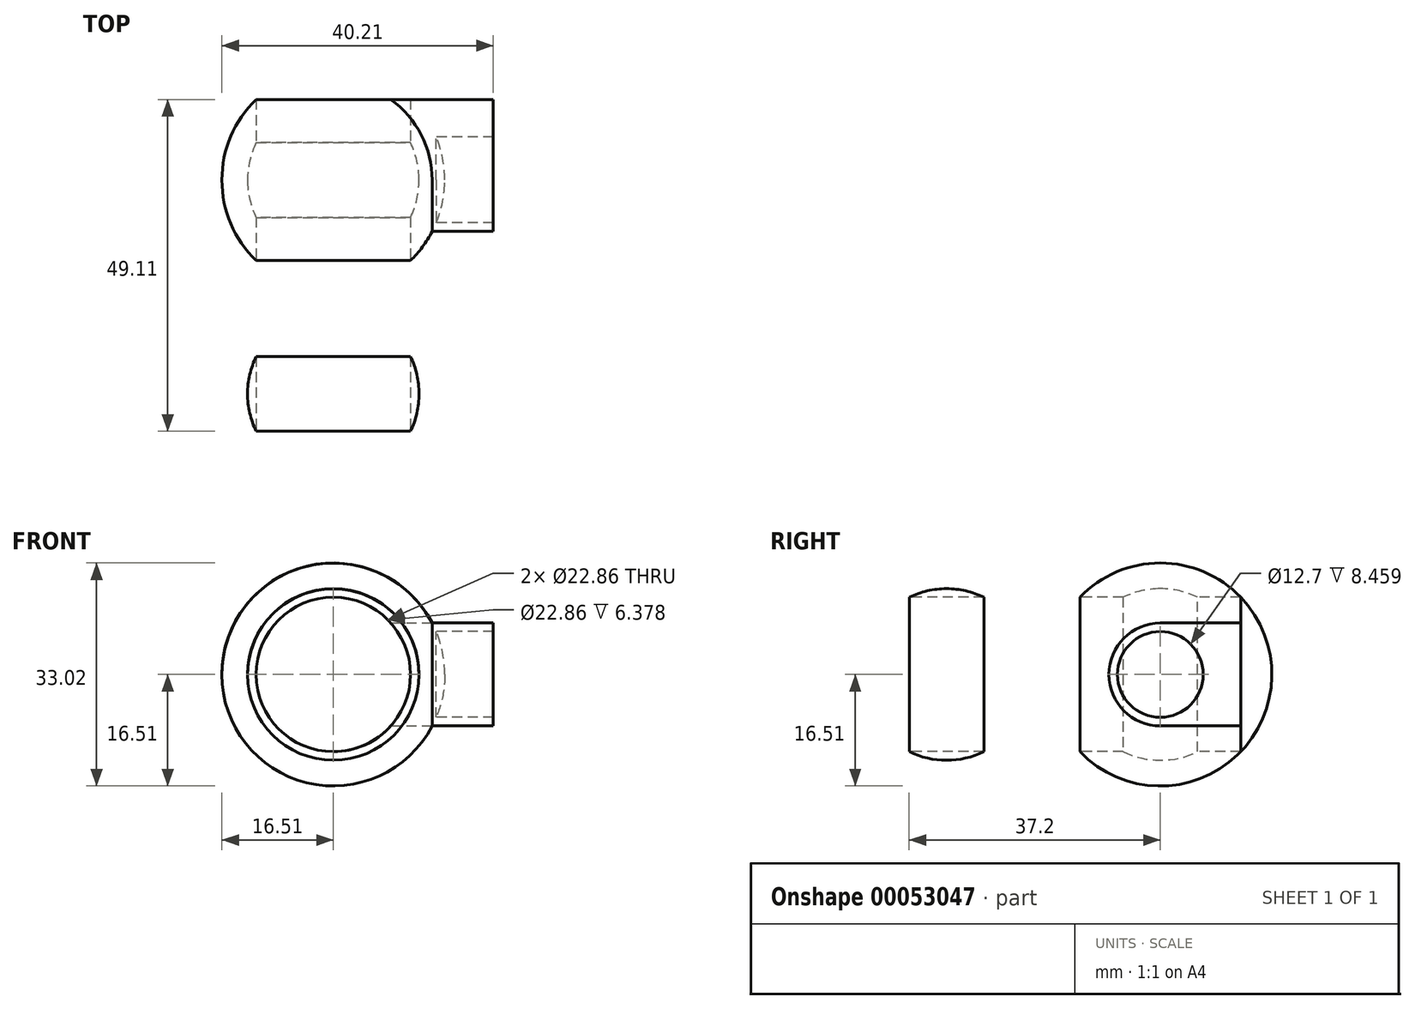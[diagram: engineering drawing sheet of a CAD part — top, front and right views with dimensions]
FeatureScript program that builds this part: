
annotation { "Feature Type Name" : "Feature", "Feature Type Description" : "" }
export const myFeature = defineFeature(function(context is Context, id is Id, definition is map)
    precondition{}
    {
        {
            var Q0;
            Q0=qCreatedBy(makeId("Front.planeOp"),FACE);
            var sketch = newSketch(context, id + "F0", { "sketchPlane" : qUnion([Q0])});
            skCircle(sketch, "E0", {"center": v(0, 0) * mm, "radius": 12.7 * mm});
            skLineSegment(sketch, "E1.rect.top", {"start": v(23.7, 6.35) * mm, "end": v(11, 6.35) * mm});
            skLineSegment(sketch, "E1.rect.left", {"start": v(23.7, 0) * mm, "end": v(23.7, 6.35) * mm});
            skLineSegment(sketch, "E2", {"start": v(-12.7, 0) * mm, "end": v(23.7, 0) * mm});
            skArc(sketch, "E3", {"start": v(13.97, 0) * mm, "mid": v(0, 13.97) * mm, "end": v(-13.97, 0) * mm});
            skArc(sketch, "E4", {"start": v(16.51, 0) * mm, "mid": v(0, 16.51) * mm, "end": v(-16.51, 0) * mm});
            skLineSegment(sketch, "E5", {"start": v(-12.7, 0) * mm, "end": v(-16.51, 0) * mm});
            skPoint(sketch, "E6", {"position": v(13.97, 0) * mm});
            skPoint(sketch, "E7", {"position": v(16.51, 0) * mm});
            skLineSegment(sketch, "E8", {"start": v(10.16, 7.62) * mm, "end": v(23.7, 7.62) * mm});
            skLineSegment(sketch, "E9", {"start": v(23.7, 7.62) * mm, "end": v(23.7, 6.35) * mm});
            skCircle(sketch, "E10", {"center": v(0, 0) * mm, "radius": 11.43 * mm});
            skSolve(sketch);
        }
        {
            var Q0;
            {var subQ0=sQuery(id+"F0.wireOp",EDGE,"E1.rect.top");var subQ1=sQuery(id+"F0.wireOp",EDGE,"E0");var subQ2=makeQuery(id+"F0.imprint","INTERSECT",VERTEX,{"derivedFrom":[subQ1,subQ0]});Q0=makeQuery(id+"F0.imprint","IMPRINT",FACE,{"disambiguationData":[TD([[makeQuery(id+"F0.imprint","IMPRINT",EDGE,{"disambiguationData":[TD([[subQ2,1.0]])],"derivedFrom":subQ1}),-1.0]])]});}
            var Q1;
            {var subQ0=sQuery(id+"F0.wireOp",EDGE,"E4");var subQ1=sQuery(id+"F0.wireOp",EDGE,"E1.rect.top");var subQ2=makeQuery(id+"F0.imprint","INTERSECT",VERTEX,{"derivedFrom":[subQ1,subQ0]});Q1=makeQuery(id+"F0.imprint","IMPRINT",FACE,{"disambiguationData":[TD([[makeQuery(id+"F0.imprint","IMPRINT",EDGE,{"disambiguationData":[TD([[subQ2,-1.0]])],"derivedFrom":subQ1}),1.0]])]});}
            var Q2;
            {var subQ0=sQuery(id+"F0.wireOp",EDGE,"E1.rect.top");var subQ1=sQuery(id+"F0.wireOp",EDGE,"E0");var subQ2=makeQuery(id+"F0.imprint","INTERSECT",VERTEX,{"derivedFrom":[subQ1,subQ0]});Q2=makeQuery(id+"F0.imprint","IMPRINT",FACE,{"disambiguationData":[TD([[makeQuery(id+"F0.imprint","IMPRINT",EDGE,{"disambiguationData":[TD([[subQ2,1.0]])],"derivedFrom":subQ0}),-1.0]])]});}
            var Q3;
            {var subQ0=sQuery(id+"F0.wireOp",EDGE,"E4");var subQ1=sQuery(id+"F0.wireOp",EDGE,"E1.rect.top");var subQ2=makeQuery(id+"F0.imprint","INTERSECT",VERTEX,{"derivedFrom":[subQ1,subQ0]});Q3=makeQuery(id+"F0.imprint","IMPRINT",FACE,{"disambiguationData":[TD([[makeQuery(id+"F0.imprint","IMPRINT",EDGE,{"disambiguationData":[TD([[subQ2,-1.0]])],"derivedFrom":subQ1}),-1.0]])]});}
            var Q4;
            {var subQ0=sQuery(id+"F0.wireOp",EDGE,"E9");Q4=makeQuery(id+"F0.imprint","IMPRINT",FACE,{"disambiguationData":[TD([[makeQuery(id+"F0.imprint","IMPRINT",EDGE,{"derivedFrom":subQ0}),-1.0]])]});}
            var Q5;
            {var subQ0=sQuery(id+"F0.wireOp",EDGE,"E5");var subQ5=sQuery(id+"F0.wireOp",EDGE,"E3");var subQ6=makeQuery(id+"F0.imprint","INTERSECT",VERTEX,{"derivedFrom":[subQ5,subQ0]});Q5=makeQuery(id+"F0.imprint","IMPRINT",FACE,{"disambiguationData":[TD([[makeQuery(id+"F0.imprint","IMPRINT",EDGE,{"disambiguationData":[TD([[subQ6,1.0]])],"derivedFrom":subQ5}),1.0]])]});}
            var Q6;
            {var subQ0=sQuery(id+"F0.wireOp",EDGE,"E5");var subQ1=sQuery(id+"F0.wireOp",EDGE,"E3");var subQ2=makeQuery(id+"F0.imprint","INTERSECT",VERTEX,{"derivedFrom":[subQ1,subQ0]});Q6=makeQuery(id+"F0.imprint","IMPRINT",FACE,{"disambiguationData":[TD([[makeQuery(id+"F0.imprint","IMPRINT",EDGE,{"disambiguationData":[TD([[subQ2,1.0]])],"derivedFrom":subQ1}),-1.0]])]});}
            var Q7;
            Q7=sQuery(id+"F0.wireOp",EDGE,"E2");
            revolve(context, id + "F1", {"entities" : qUnion([Q0, Q1, Q2, Q3, Q4, Q5, Q6]), "axis" : qUnion([Q7]), "revolveType" : RevolveType.FULL});
        }
        {
            var Q0;
            {var subQ0=sQuery(id+"F0.wireOp",EDGE,"E0");var subQ1=makeQuery(id+"F0.imprint","INTERSECT",VERTEX,{"derivedFrom":[subQ0,sQuery(id+"F0.wireOp",EDGE,"E1.rect.top")]});Q0=makeQuery(id+"F0.imprint","IMPRINT",FACE,{"disambiguationData":[TD([[makeQuery(id+"F0.imprint","IMPRINT",EDGE,{"disambiguationData":[TD([[subQ1,1.0]])],"derivedFrom":subQ0}),1.0]])]});}
            var Q1;
            Q1=sQuery(id+"F0.wireOp",EDGE,"E2");
            revolve(context, id + "F2", {"entities" : qUnion([Q0]), "axis" : qUnion([Q1]), "revolveType" : RevolveType.FULL});
        }
        {
            var Q0;
            {var subQ0=sQuery(id+"F0.wireOp",EDGE,"E10");var subQ1=sQuery(id+"F0.wireOp",EDGE,"E2");var subQ2=makeQuery(id+"F0.imprint","INTERSECT",VERTEX,{"disambiguationData":[OD(0.0)],"derivedFrom":[subQ1,subQ0]});Q0=makeQuery(id+"F0.imprint","IMPRINT",FACE,{"disambiguationData":[TD([[makeQuery(id+"F0.imprint","IMPRINT",EDGE,{"disambiguationData":[TD([[subQ2,-1.0]])],"derivedFrom":subQ1}),1.0]])]});}
            var Q1;
            {var subQ0=sQuery(id+"F0.wireOp",EDGE,"E10");var subQ1=sQuery(id+"F0.wireOp",EDGE,"E2");var subQ2=makeQuery(id+"F0.imprint","INTERSECT",VERTEX,{"disambiguationData":[OD(0.0)],"derivedFrom":[subQ1,subQ0]});Q1=makeQuery(id+"F0.imprint","IMPRINT",FACE,{"disambiguationData":[TD([[makeQuery(id+"F0.imprint","IMPRINT",EDGE,{"disambiguationData":[TD([[subQ2,-1.0]])],"derivedFrom":subQ1}),-1.0]])]});}
            extrude(context, id + "F3", {"entities" : qUnion([Q0, Q1]), "operationType" : NewBodyOperationType.REMOVE, "endBound" : BoundingType.THROUGH_ALL, "oppositeDirection" : true, "depth" : 25.4 * mm, "hasSecondDirection" : true, "secondDirectionBound" : BoundingType.THROUGH_ALL, "secondDirectionOppositeDirection" : false, "secondDirectionDepth" : 25.4 * mm});
        }
        {
            var Q0;
            Q0=makeQuery(id+"F1.opRevolve","SWEPT_FACE",FACE,{"disambiguationData":[OSD([sQuery(id+"F0.wireOp",EDGE,"E9")])]});
            var sketch = newSketch(context, id + "F4", { "sketchPlane" : qUnion([Q0])});
            skPoint(sketch, "E11.0", {"position": v(0, 0) * mm});
            skCircle(sketch, "E12.0", {"center": v(0, 0) * mm, "radius": 6.35 * mm});
            skLineSegment(sketch, "E13.0", {"start": v(11.91, -7.62) * mm, "end": v(11.91, 7.62) * mm});
            skLineSegment(sketch, "E14", {"start": v(0, 7.62) * mm, "end": v(11.91, 7.62) * mm});
            skLineSegment(sketch, "E15", {"start": v(0, -7.62) * mm, "end": v(11.91, -7.62) * mm});
            skPoint(sketch, "E16.orphan", {"position": v(11.91, 11.43) * mm});
            skPoint(sketch, "E17.orphan", {"position": v(11.91, -11.43) * mm});
            skSolve(sketch);
        }
        {
            var Q0;
            Q0=makeQuery(id+"F4.imprint","IMPRINT",FACE,{"disambiguationData":[TD([[makeQuery(id+"F4.imprint","IMPRINT",EDGE,{"derivedFrom":sQuery(id+"F4.wireOp",EDGE,"E13.0")}),1.0]])]});
            var Q1;
            Q1=makeQuery(id+"F1.opRevolve","SWEPT_BODY",BODY,{"disambiguationData":[OSD([sQuery(id+"F0.wireOp",EDGE,"E0"),sQuery(id+"F0.wireOp",EDGE,"E1.rect.top"),sQuery(id+"F0.wireOp",EDGE,"E2"),sQuery(id+"F0.wireOp",EDGE,"E4"),sQuery(id+"F0.wireOp",EDGE,"E5"),sQuery(id+"F0.wireOp",EDGE,"E8"),sQuery(id+"F0.wireOp",EDGE,"E9")])]});
            extrude(context, id + "F5", {"entities" : qUnion([Q0]), "operationType" : NewBodyOperationType.ADD, "endBound" : BoundingType.UP_TO_BODY, "oppositeDirection" : true, "endBoundEntityBody" : qUnion([Q1]), "depth" : 25.4 * mm});
        }
        {
            var Q0;
            Q0=makeQuery(id+"F2.opRevolve","SWEPT_BODY",BODY,{"disambiguationData":[OSD([sQuery(id+"F0.wireOp",EDGE,"E0"),sQuery(id+"F0.wireOp",EDGE,"E2")])]});
            transform(context, id + "F6", {"entities" : qUnion([Q0]), "transformType" : TransformType.TRANSLATION_3D, "dx" : 0 * mm, "dy" : -31.66 * mm, "dz" : 0 * mm, "makeCopy" : false});
        }
    });
